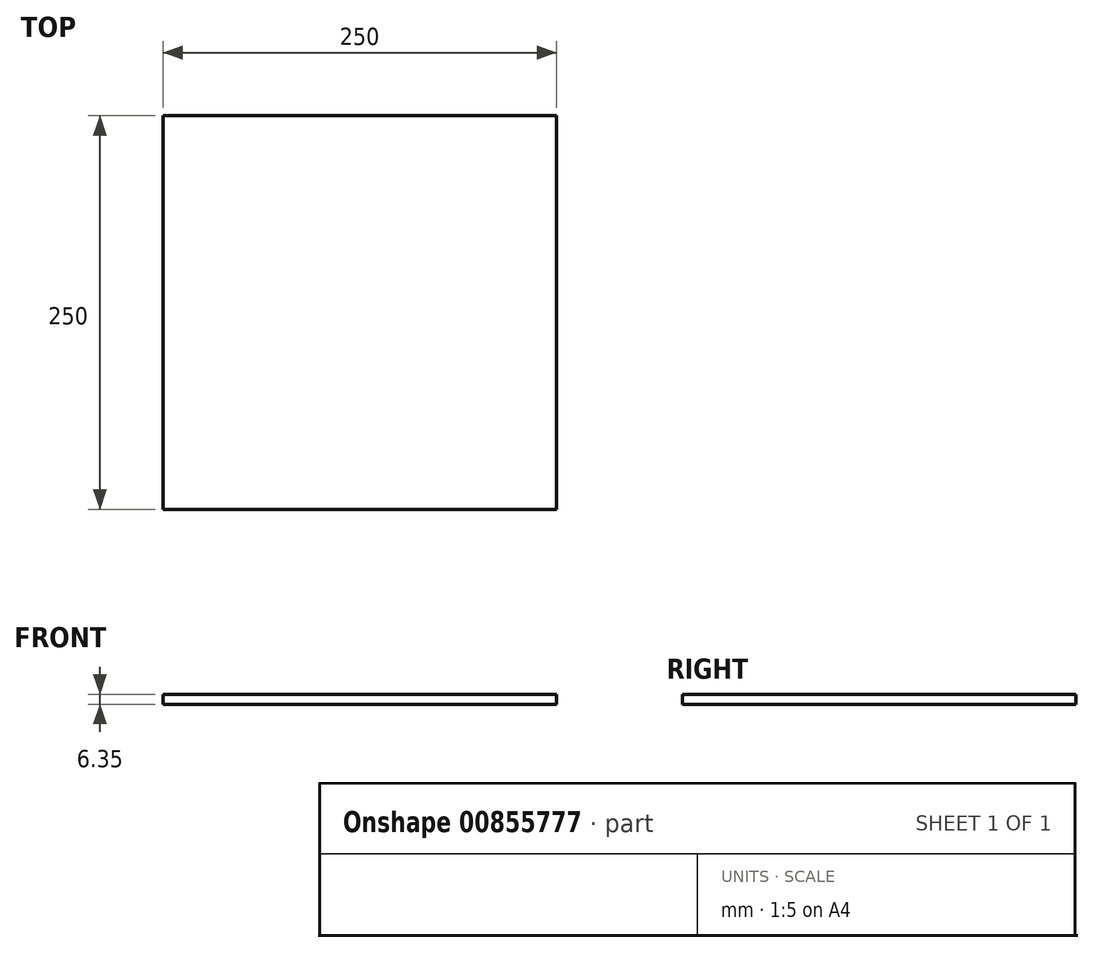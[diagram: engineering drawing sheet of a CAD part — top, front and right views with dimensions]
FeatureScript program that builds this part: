
annotation { "Feature Type Name" : "Feature", "Feature Type Description" : "" }
export const myFeature = defineFeature(function(context is Context, id is Id, definition is map)
    precondition{}
    {
        {
            var Q0;
            Q0=qCreatedBy(makeId("Top.planeOp"),FACE);
            var sketch = newSketch(context, id + "F0", { "sketchPlane" : qUnion([Q0])});
            skLineSegment(sketch, "E0.bottom", {"start": v(-125, 125) * mm, "end": v(125, 125) * mm});
            skLineSegment(sketch, "E0.top", {"start": v(-125, -125) * mm, "end": v(125, -125) * mm});
            skLineSegment(sketch, "E0.left", {"start": v(-125, 125) * mm, "end": v(-125, -125) * mm});
            skLineSegment(sketch, "E0.right", {"start": v(125, 125) * mm, "end": v(125, -125) * mm});
            skPoint(sketch, "E0.middle", {"position": v(0, 0) * mm});
            skSolve(sketch);
        }
        {
            var Q0;
            Q0=makeQuery(id+"F0.imprint","IMPRINT",FACE,{"disambiguationData":[TD([[makeQuery(id+"F0.imprint","IMPRINT",EDGE,{"derivedFrom":sQuery(id+"F0.wireOp",EDGE,"E0.bottom")}),-1.0]])]});
            extrude(context, id + "F1", {"entities" : qUnion([Q0]), "depth" : 6.35 * mm, "offsetDistance" : 25 * mm});
        }
    });
